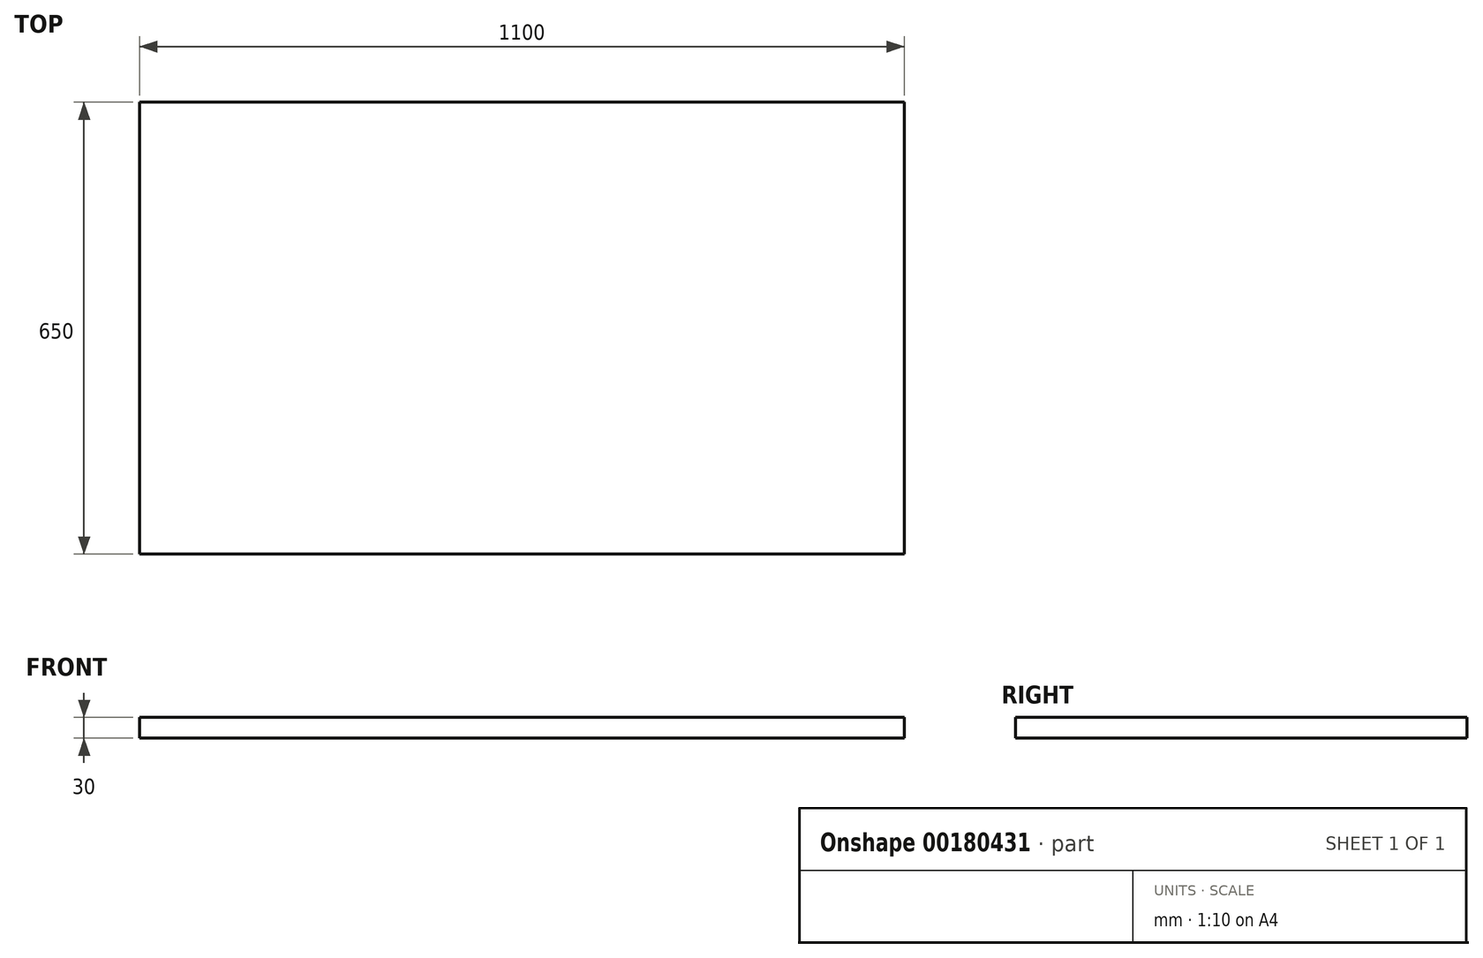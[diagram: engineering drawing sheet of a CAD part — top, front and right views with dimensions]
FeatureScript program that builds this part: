
annotation { "Feature Type Name" : "Feature", "Feature Type Description" : "" }
export const myFeature = defineFeature(function(context is Context, id is Id, definition is map)
    precondition{}
    {
        {
            var Q0;
            Q0=qCreatedBy(makeId("Top.planeOp"),FACE);
            var sketch = newSketch(context, id + "F0", { "sketchPlane" : qUnion([Q0])});
            skLineSegment(sketch, "E0.bottom", {"start": v(-648.34, -162.9) * mm, "end": v(451.66, -162.9) * mm});
            skLineSegment(sketch, "E0.top", {"start": v(-648.34, 487.1) * mm, "end": v(451.66, 487.1) * mm});
            skLineSegment(sketch, "E0.left", {"start": v(-648.34, -162.9) * mm, "end": v(-648.34, 487.1) * mm});
            skLineSegment(sketch, "E0.right", {"start": v(451.66, -162.9) * mm, "end": v(451.66, 487.1) * mm});
            skSolve(sketch);
        }
        {
            var Q0;
            Q0=makeQuery(id+"F0.imprint","IMPRINT",FACE,{"disambiguationData":[TD([[makeQuery(id+"F0.imprint","IMPRINT",EDGE,{"derivedFrom":sQuery(id+"F0.wireOp",EDGE,"E0.bottom")}),1.0]])]});
            extrude(context, id + "F1", {"entities" : qUnion([Q0]), "depth" : 30 * mm});
        }
    });
